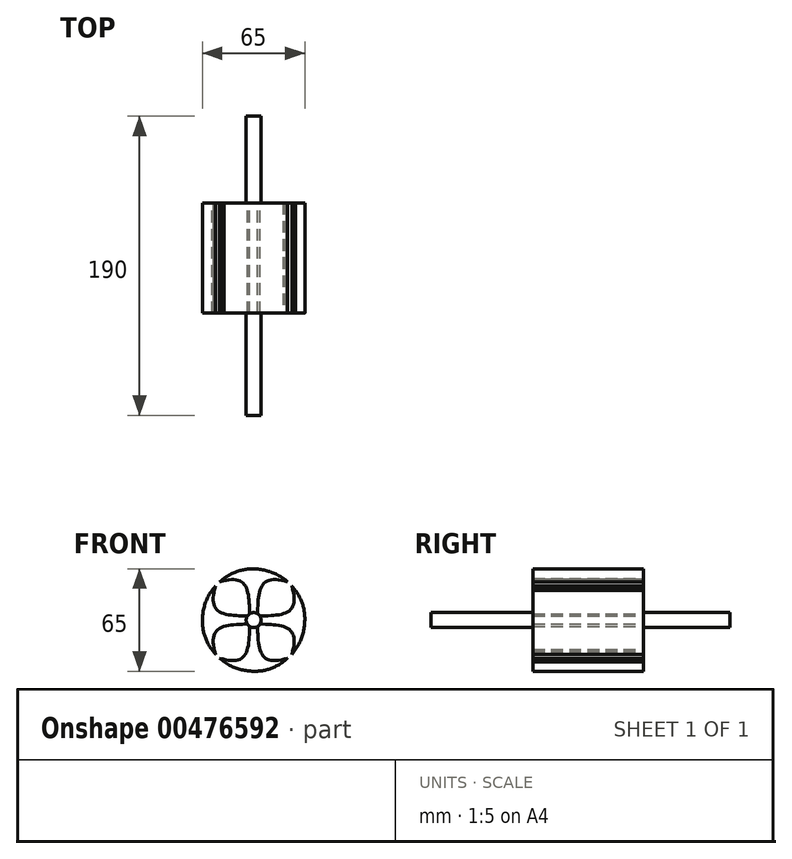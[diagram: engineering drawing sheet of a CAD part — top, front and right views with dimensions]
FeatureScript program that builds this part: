
annotation { "Feature Type Name" : "Feature", "Feature Type Description" : "" }
export const myFeature = defineFeature(function(context is Context, id is Id, definition is map)
    precondition{}
    {
        {
            var Q0;
            Q0=qCreatedBy(makeId("Front.planeOp"),FACE);
            var sketch = newSketch(context, id + "F0", { "sketchPlane" : qUnion([Q0])});
            skCircle(sketch, "E0", {"center": v(0, 0) * mm, "radius": 4.75 * mm});
            skSolve(sketch);
        }
        {
            var Q0;
            Q0=makeQuery(id+"F0.imprint","IMPRINT",FACE,{"disambiguationData":[TD([[makeQuery(id+"F0.imprint","IMPRINT",EDGE,{"derivedFrom":sQuery(id+"F0.wireOp",EDGE,"E0")}),1.0]])]});
            extrude(context, id + "F1", {"entities" : qUnion([Q0]), "depth" : 160 * mm, "hasSecondDirection" : true, "secondDirectionOppositeDirection" : true, "secondDirectionDepth" : 30 * mm});
        }
        {
            var Q0;
            Q0=qCreatedBy(makeId("Top.planeOp"),FACE);
            var sketch = newSketch(context, id + "F2", { "sketchPlane" : qUnion([Q0])});
            skPoint(sketch, "E1", {"position": v(0, -25) * mm});
            skLineSegment(sketch, "E2", {"start": v(0, -25) * mm, "end": v(19.6, -25) * mm});
            skPoint(sketch, "E3", {"position": v(0, 10.23) * mm});
            skSolve(sketch);
        }
        {
            var Q0;
            Q0=qBodyType(qCreatedBy(id+"F2",EDGE),BodyType.WIRE);
            var Q1;
            Q1=qCreatedBy(makeId("Top.planeOp"),FACE);
            cPlane(context, id + "F3", {"entities" : qUnion([Q0, Q1]), "cplaneType" : CPlaneType.LINE_ANGLE, "offset" : 25 * mm, "angle" : 90 * degree, "width" : 150 * mm, "height" : 150 * mm});
        }
        {
            var Q0;
            Q0=qCreatedBy(id+"F3.planeOp",FACE);
            var sketch = newSketch(context, id + "F4", { "sketchPlane" : qUnion([Q0])});
            skFitSpline(sketch, "E4", {"points": [v(-21.67, 24.22) * mm, v(-5.3, 21.72) * mm, v(-2.54, 0) * mm], "startDerivative": vector(55.1, 15.96) * mm, "endDerivative": vector(0.69, -36.18) * mm});
            skFitSpline(sketch, "E5.MirrorCS", {"points": [v(21.67, 24.22) * mm, v(5.3, 21.72) * mm, v(2.54, 0) * mm], "startDerivative": vector(-55.1, 15.96) * mm, "endDerivative": vector(-0.69, -36.18) * mm});
            skFitSpline(sketch, "E6", {"points": [v(21.67, 24.22) * mm, v(0, 32.5) * mm, v(-21.67, 24.22) * mm], "startDerivative": vector(-45.02, 38.92) * mm, "endDerivative": vector(-41.21, -36.13) * mm});
            skPoint(sketch, "E7.center", {"position": v(0, 0) * mm});
            skLineSegment(sketch, "E8", {"start": v(2.54, 0) * mm, "end": v(-2.54, 0) * mm});
            skFitSpline(sketch, "E9", {"points": [v(18.43, 26.77) * mm, v(19.85, 25.73) * mm, v(21.67, 24.22) * mm], "startDerivative": vector(2.96, -2.15) * mm, "endDerivative": vector(3.5, -2.92) * mm});
            skFitSpline(sketch, "E10", {"points": [v(19.85, 25.73) * mm, v(20.79, 24.97) * mm, v(21.67, 24.22) * mm], "startDerivative": vector(1.86, -1.51) * mm, "endDerivative": vector(1.76, -1.5) * mm});
            skFitSpline(sketch, "E11", {"points": [v(0, 32.5) * mm, v(-10.55, 30.7) * mm, v(-21.67, 24.22) * mm], "startDerivative": vector(-22.48, -1.07) * mm, "endDerivative": vector(-20.88, -15.26) * mm});
            skSolve(sketch);
        }
        {
            var Q0;
            Q0=qSketchRegion(id+"F4",true);
            extrude(context, id + "F5", {"entities" : qUnion([Q0]), "operationType" : NewBodyOperationType.ADD, "oppositeDirection" : true, "depth" : 70 * mm});
        }
        {
            var Q0;
            Q0=qCreatedBy(makeId("Top.planeOp"),FACE);
            var sketch = newSketch(context, id + "F6", { "sketchPlane" : qUnion([Q0])});
            skPoint(sketch, "E12", {"position": v(0, -69.6) * mm});
            skLineSegment(sketch, "E13", {"start": v(0, -24.78) * mm, "end": v(0, -69.6) * mm});
            skSolve(sketch);
        }
        {
            var Q0;
            Q0=makeQuery(id+"F1.opExtrude","SWEPT_BODY",BODY,{"disambiguationData":[OSD([sQuery(id+"F0.wireOp",EDGE,"E0")])]});
            var Q1;
            Q1=sQuery(id+"F6.wireOp",EDGE,"E13");
            circularPattern(context, id + "F7", {"operationType" : NewBodyOperationType.ADD, "entities" : qUnion([Q0]), "axis" : qUnion([Q1]), "angle" : 90 * degree, "instanceCount" : 4});
        }
    });
